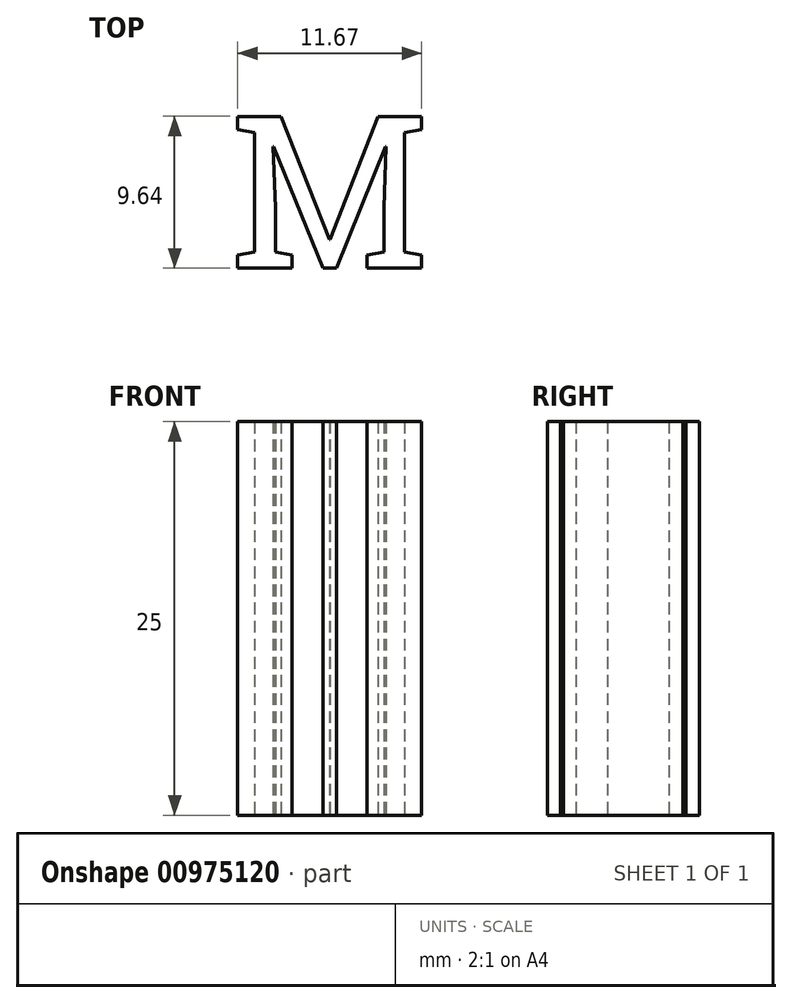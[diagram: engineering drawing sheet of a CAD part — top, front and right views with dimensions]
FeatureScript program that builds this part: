
annotation { "Feature Type Name" : "Feature", "Feature Type Description" : "" }
export const myFeature = defineFeature(function(context is Context, id is Id, definition is map)
    precondition{}
    {
        {
            var Q0;
            Q0=qCreatedBy(makeId("Top.planeOp"),FACE);
            var sketch = newSketch(context, id + "F0", { "sketchPlane" : qUnion([Q0])});
            skText(sketch, "E0", { "text": "M", "fontName": "RobotoSlab-Regular.ttf"});
            const initialGuessF0  = {"E0": [-0.00627, 0.02342, 1, 0, 0.00976]};
            skSetInitialGuess(sketch, initialGuessF0);
            skSolve(sketch);
        }
        {
            var Q0;
            Q0 = qSketchRegion(id + "F0", true);
            extrude(context, id + "F1", {"entities" : qUnion([Q0]), "depth" : 25 * mm, "offsetDistance" : 25 * mm});
        }
    });
